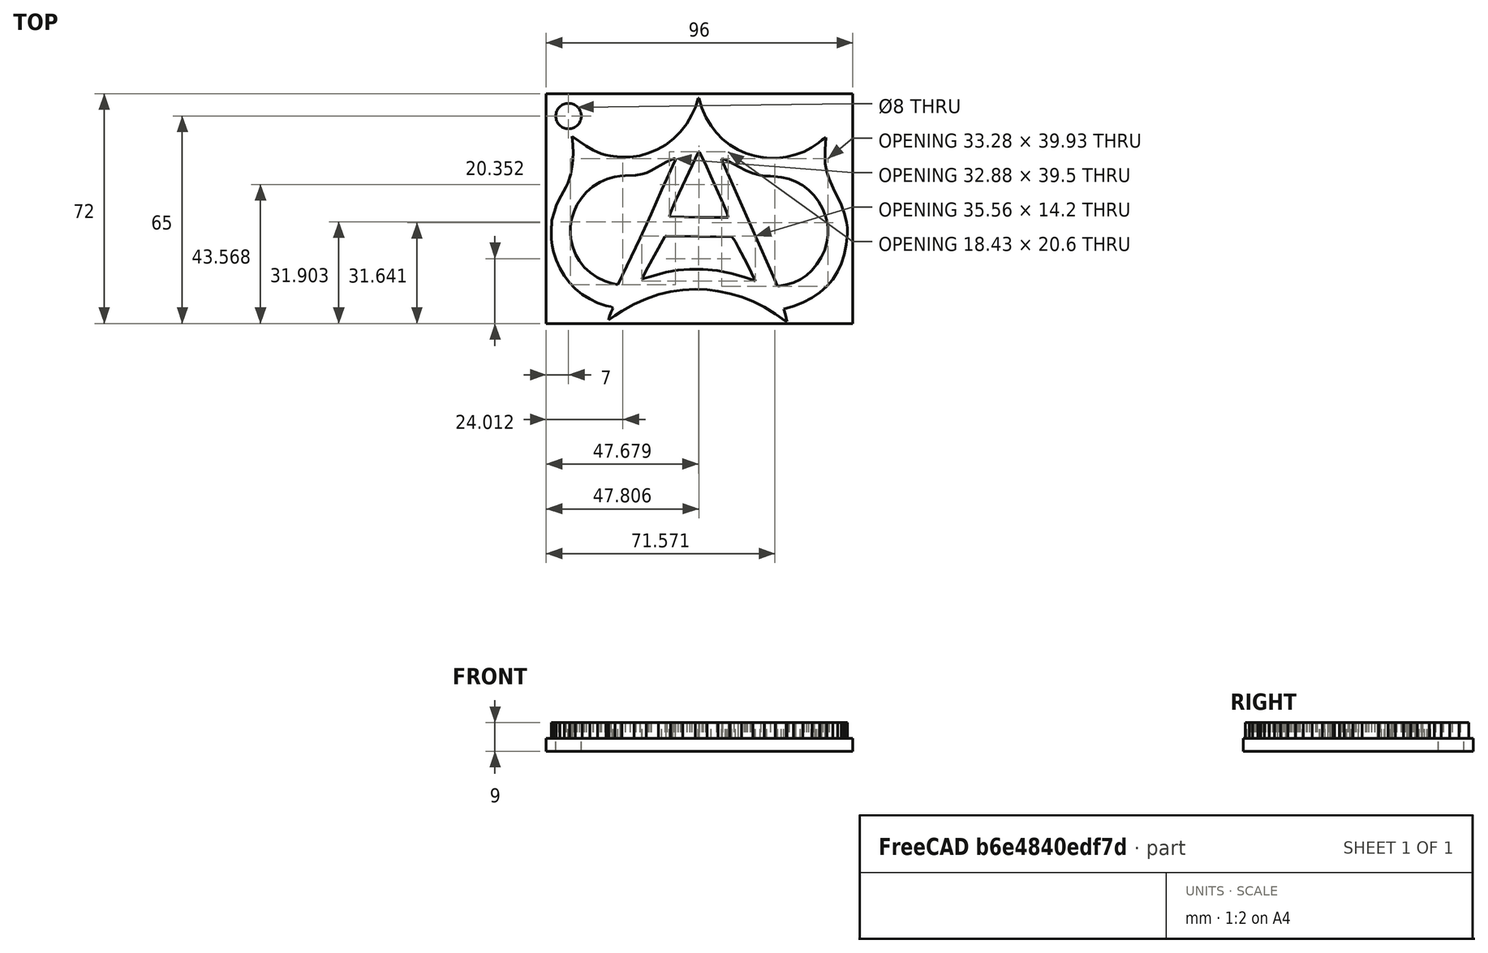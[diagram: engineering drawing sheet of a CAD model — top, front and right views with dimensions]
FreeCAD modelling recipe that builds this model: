
FCSTD DOCUMENT  (FreeCAD 0.17R13494 (Git))
Label: marco
License: All rights reserved
LicenseURL: http://en.wikipedia.org/wiki/All_rights_reserved
objects: Part::Feature×1, Part::Box×1, Part::Cylinder×1, Part::Cut×1, Part::FeaturePython×1
note: 5 computed .brp shape members not serialized (recipe doc carries the construction recipe); baked Part::Feature solids carry a one-line shape summary decoded from their .brp

FEATURE [Part::Feature] Solid
  Placement = pos=(-82,200,-1) rot=(0,0,1;0rad)
  shape: bbox 92.71 x 70.02 x 5 mm, 242 faces (baked)
FEATURE [Part::Box] Box001  label="Cubo001"
  AttacherType = Attacher::AttachEngine3D
  Height = 4
  Length = 96
  Placement = pos=(-46,-37,-5) rot=(0,0,1;0rad)
  Width = 72
FEATURE [Part::Cylinder] Cylinder  label="Cilindro"
  Angle = 360
  AttacherType = Attacher::AttachEngine3D
  Height = 10
  Placement = pos=(-39,28,-8) rot=(0,0,1;0rad)
  Radius = 4
FEATURE [Part::Cut] Cut
  Base = -> Box001
  Tool = -> Cylinder
FEATURE [Part::FeaturePython] Clone  label="Solid001"  # Draft clone (typed FeaturePython)
  AttacherType = Attacher::AttachEngine3D
  Fuse = false
  Objects = -> [Solid]
  Placement = pos=(-82,200,-1) rot=(0,0,1;0rad)
  Scale = (1,1,1)
